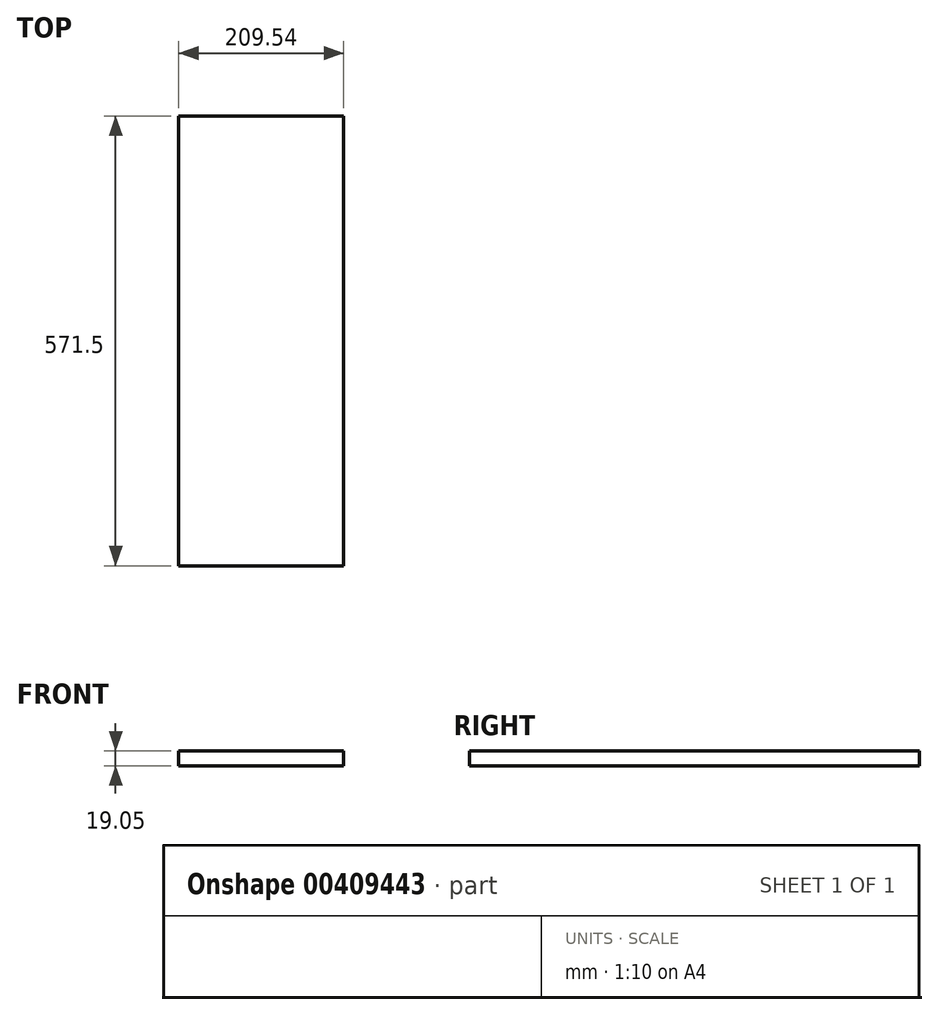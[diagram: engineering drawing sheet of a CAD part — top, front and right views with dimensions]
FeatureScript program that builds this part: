
annotation { "Feature Type Name" : "Feature", "Feature Type Description" : "" }
export const myFeature = defineFeature(function(context is Context, id is Id, definition is map)
    precondition{}
    {
        {
            var Q0;
            Q0=qCreatedBy(makeId("Top.planeOp"),FACE);
            var sketch = newSketch(context, id + "F0", { "sketchPlane" : qUnion([Q0])});
            skLineSegment(sketch, "E0.bottom", {"start": v(-104.77, -285.75) * mm, "end": v(104.78, -285.75) * mm});
            skLineSegment(sketch, "E0.top", {"start": v(-104.78, 285.75) * mm, "end": v(104.78, 285.75) * mm});
            skLineSegment(sketch, "E0.left", {"start": v(-104.77, -285.75) * mm, "end": v(-104.78, 285.75) * mm});
            skLineSegment(sketch, "E0.right", {"start": v(104.78, -285.75) * mm, "end": v(104.78, 285.75) * mm});
            skPoint(sketch, "E0.middle", {"position": v(0, 0) * mm});
            skSolve(sketch);
        }
        {
            var Q0;
            Q0=makeQuery(id+"F0.imprint","IMPRINT",FACE,{"disambiguationData":[TD([[makeQuery(id+"F0.imprint","IMPRINT",EDGE,{"derivedFrom":sQuery(id+"F0.wireOp",EDGE,"E0.bottom")}),1.0]])]});
            extrude(context, id + "F1", {"entities" : qUnion([Q0]), "depth" : 19.05 * mm});
        }
    });
